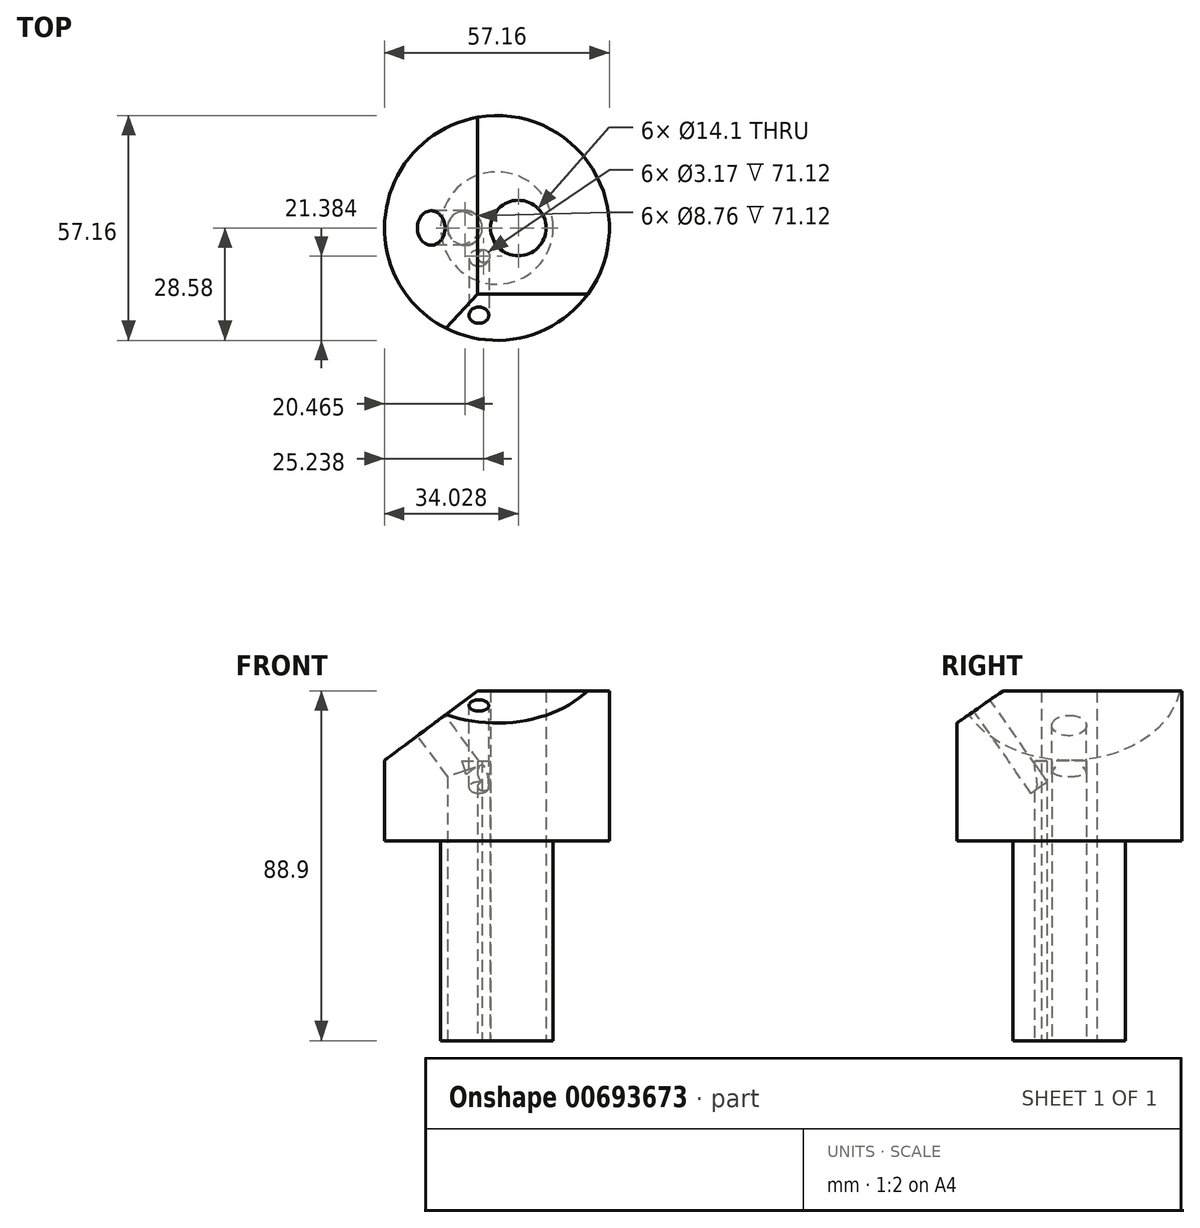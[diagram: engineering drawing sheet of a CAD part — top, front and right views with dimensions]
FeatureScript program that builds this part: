
annotation { "Feature Type Name" : "Feature", "Feature Type Description" : "" }
export const myFeature = defineFeature(function(context is Context, id is Id, definition is map)
    precondition{}
    {
        {
            var Q0;
            Q0=qCreatedBy(makeId("Front.planeOp"),FACE);
            var sketch = newSketch(context, id + "F0", { "sketchPlane" : qUnion([Q0])});
            skLineSegment(sketch, "E0.bottom", {"start": v(0, 0) * mm, "end": v(14.29, 0) * mm});
            skLineSegment(sketch, "E0.top", {"start": v(0, 50.8) * mm, "end": v(14.29, 50.8) * mm});
            skLineSegment(sketch, "E0.left", {"start": v(0, 0) * mm, "end": v(0, 50.8) * mm});
            skLineSegment(sketch, "E0.right", {"start": v(14.29, 0) * mm, "end": v(14.29, 50.8) * mm});
            skLineSegment(sketch, "E1.bottom", {"start": v(0, 50.8) * mm, "end": v(28.57, 50.8) * mm});
            skLineSegment(sketch, "E1.top", {"start": v(0, 88.9) * mm, "end": v(28.57, 88.9) * mm});
            skLineSegment(sketch, "E1.left", {"start": v(0, 50.8) * mm, "end": v(0, 88.9) * mm});
            skLineSegment(sketch, "E1.right", {"start": v(28.57, 50.8) * mm, "end": v(28.57, 88.9) * mm});
            skSolve(sketch);
        }
        {
            var Q0;
            Q0=makeQuery(id+"F0.imprint","IMPRINT",FACE,{"disambiguationData":[TD([[makeQuery(id+"F0.imprint","IMPRINT",EDGE,{"derivedFrom":sQuery(id+"F0.wireOp",EDGE,"E1.top")}),-1.0]])]});
            var Q1;
            Q1=makeQuery(id+"F0.imprint","IMPRINT",FACE,{"disambiguationData":[TD([[makeQuery(id+"F0.imprint","IMPRINT",EDGE,{"derivedFrom":sQuery(id+"F0.wireOp",EDGE,"E0.bottom")}),1.0]])]});
            var Q2;
            Q2 = qConstructionFilter(qBodyType(qCreatedBy(id + "F0" ,EDGE), BodyType.WIRE), ConstructionObject.NO);
            var Q3;
            Q3=sQuery(id+"F0.wireOp",EDGE,"E0.left");
            revolve(context, id + "F1", {"entities" : qUnion([Q0, Q1]), "surfaceEntities" : qUnion([Q2]), "axis" : qUnion([Q3]), "revolveType" : RevolveType.FULL});
        }
        {
            var Q0;
            Q0=makeQuery(id+"F1.opRevolve","SWEPT_FACE",FACE,{"disambiguationData":[OSD([sQuery(id+"F0.wireOp",EDGE,"E0.bottom")])]});
            var sketch = newSketch(context, id + "F2", { "sketchPlane" : qUnion([Q0])});
            skCircle(sketch, "E2", {"center": v(5.45, 0) * mm, "radius": 7.05 * mm});
            skCircle(sketch, "E3", {"center": v(0, 0) * mm, "radius": 12.5 * mm, "construction": true});
            skCircle(sketch, "E4", {"center": v(-8.12, 0) * mm, "radius": 4.38 * mm});
            skCircle(sketch, "E5", {"center": v(-3.34, 7.2) * mm, "radius": 1.59 * mm});
            skSolve(sketch);
        }
        {
            var Q0;
            Q0=makeQuery(id+"F2.imprint","IMPRINT",FACE,{"disambiguationData":[TD([[makeQuery(id+"F2.imprint","IMPRINT",EDGE,{"derivedFrom":sQuery(id+"F2.wireOp",EDGE,"E2")}),1.0]])]});
            extrude(context, id + "F3", {"entities" : qUnion([Q0]), "operationType" : NewBodyOperationType.REMOVE, "endBound" : BoundingType.THROUGH_ALL, "oppositeDirection" : true, "depth" : 25.4 * mm, "offsetDistance" : 25.4 * mm});
        }
        {
            var Q0;
            Q0=makeQuery(id+"F2.imprint","IMPRINT",FACE,{"disambiguationData":[TD([[makeQuery(id+"F2.imprint","IMPRINT",EDGE,{"derivedFrom":sQuery(id+"F2.wireOp",EDGE,"E4")}),1.0]])]});
            var Q1;
            Q1=makeQuery(id+"F2.imprint","IMPRINT",FACE,{"disambiguationData":[TD([[makeQuery(id+"F2.imprint","IMPRINT",EDGE,{"derivedFrom":sQuery(id+"F2.wireOp",EDGE,"E5")}),1.0]])]});
            var Q2;
            Q2=sQuery(id+"F2.wireOp",EDGE,"E4");
            extrude(context, id + "F4", {"entities" : qUnion([Q0, Q1]), "operationType" : NewBodyOperationType.REMOVE, "surfaceEntities" : qUnion([Q2]), "oppositeDirection" : true, "depth" : 71.12 * mm, "offsetDistance" : 25.4 * mm});
        }
        {
            var Q0;
            Q0=qCreatedBy(makeId("Front.planeOp"),FACE);
            var sketch = newSketch(context, id + "F5", { "sketchPlane" : qUnion([Q0])});
            skLineSegment(sketch, "E6", {"start": v(0, 92.54) * mm, "end": v(-31.22, 69.21) * mm});
            skLineSegment(sketch, "E7", {"start": v(-31.22, 69.21) * mm, "end": v(-31.22, 92.5) * mm});
            skLineSegment(sketch, "E8", {"start": v(-31.22, 92.5) * mm, "end": v(0, 92.54) * mm});
            skSolve(sketch);
        }
        {
            var Q0;
            Q0=makeQuery(id+"F5.imprint","IMPRINT",FACE,{"disambiguationData":[TD([[makeQuery(id+"F5.imprint","IMPRINT",EDGE,{"derivedFrom":sQuery(id+"F5.wireOp",EDGE,"E6")}),-1.0]])]});
            extrude(context, id + "F6", {"entities" : qUnion([Q0]), "operationType" : NewBodyOperationType.REMOVE, "endBound" : BoundingType.THROUGH_ALL, "oppositeDirection" : true, "depth" : 25.4 * mm, "offsetDistance" : 25.4 * mm, "hasSecondDirection" : true, "secondDirectionBound" : SecondDirectionBoundingType.THROUGH_ALL, "secondDirectionOppositeDirection" : false, "secondDirectionDepth" : 25.4 * mm});
        }
        {
            var Q0;
            Q0=makeQuery(id+"F6.boolean.opBoolean","COPY",FACE,{"derivedFrom":makeQuery(id+"F6.opExtrude","SWEPT_FACE",FACE,{"disambiguationData":[OSD([sQuery(id+"F5.wireOp",EDGE,"E6")])]})});
            var sketch = newSketch(context, id + "F7", { "sketchPlane" : qUnion([Q0])});
            skCircle(sketch, "E9", {"center": v(34.53, 0) * mm, "radius": 4.38 * mm});
            skPoint(sketch, "E9.centerSnap0", {"position": v(19.72, 0) * mm});
            skSolve(sketch);
        }
        {
            var Q0;
            Q0=makeQuery(id+"F7.imprint","IMPRINT",FACE,{"disambiguationData":[TD([[makeQuery(id+"F7.imprint","IMPRINT",EDGE,{"derivedFrom":sQuery(id+"F7.wireOp",EDGE,"E9")}),1.0]])]});
            extrude(context, id + "F8", {"entities" : qUnion([Q0]), "operationType" : NewBodyOperationType.REMOVE, "oppositeDirection" : true, "depth" : 15.24 * mm, "offsetDistance" : 25.4 * mm});
        }
        {
            var Q0;
            Q0=qCreatedBy(makeId("Right.planeOp"),FACE);
            var sketch = newSketch(context, id + "F9", { "sketchPlane" : qUnion([Q0])});
            skLineSegment(sketch, "E10", {"start": v(-11.25, 92.75) * mm, "end": v(-39.16, 73.32) * mm});
            skLineSegment(sketch, "E11", {"start": v(-39.16, 73.32) * mm, "end": v(-39.16, 97.82) * mm});
            skLineSegment(sketch, "E12", {"start": v(-39.16, 97.82) * mm, "end": v(-11.25, 92.75) * mm});
            skSolve(sketch);
        }
        {
            var Q0;
            Q0 = qSketchRegion(id + "F9", true);
            extrude(context, id + "F10", {"entities" : qUnion([Q0]), "operationType" : NewBodyOperationType.REMOVE, "endBound" : BoundingType.THROUGH_ALL, "oppositeDirection" : true, "depth" : 25.4 * mm, "offsetDistance" : 25.4 * mm, "hasSecondDirection" : true, "secondDirectionBound" : SecondDirectionBoundingType.THROUGH_ALL, "secondDirectionOppositeDirection" : false, "secondDirectionDepth" : 25.4 * mm});
        }
        {
            var Q0;
            Q0=makeQuery(id+"F10.boolean.opBoolean","COPY",FACE,{"derivedFrom":makeQuery(id+"F10.opExtrude","SWEPT_FACE",FACE,{"disambiguationData":[OSD([sQuery(id+"F9.wireOp",EDGE,"E10")])]})});
            var sketch = newSketch(context, id + "F11", { "sketchPlane" : qUnion([Q0])});
            skCircle(sketch, "E13", {"center": v(-4.58, 30.48) * mm, "radius": 2.52 * mm});
            skSolve(sketch);
        }
        {
            var Q0;
            Q0=makeQuery(id+"F11.imprint","IMPRINT",FACE,{"disambiguationData":[TD([[makeQuery(id+"F11.imprint","IMPRINT",EDGE,{"derivedFrom":sQuery(id+"F11.wireOp",EDGE,"E13")}),1.0]])]});
            var Q1;
            Q1=sQuery(id+"F11.wireOp",EDGE,"E13");
            extrude(context, id + "F12", {"entities" : qUnion([Q0]), "operationType" : NewBodyOperationType.REMOVE, "surfaceEntities" : qUnion([Q1]), "oppositeDirection" : true, "depth" : 25.4 * mm, "offsetDistance" : 25.4 * mm});
        }
    });
